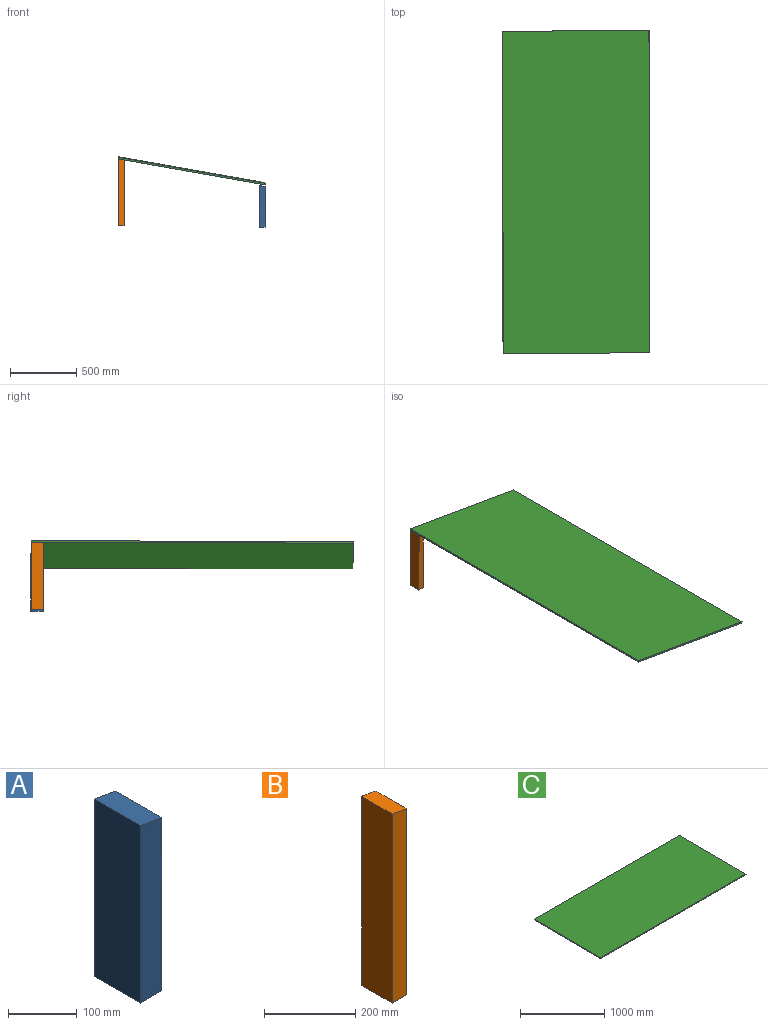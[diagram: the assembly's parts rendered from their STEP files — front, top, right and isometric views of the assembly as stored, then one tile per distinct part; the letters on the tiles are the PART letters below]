
ASSEMBLY  parts=3 mates=1
PART A: 6 faces, bbox 44.5x95.2x316.5 mm
  f0: plane 316.48x95.25mm, normal (-1,0,0), area 30144.9mm2, adj f1,f3,f4,f5
  f1: plane 95.25x44.45mm, normal (0.17,0,0.98), area 4299.2mm2, adj f0,f2,f3,f4
  f2: plane 308.65x95.25mm, normal (1,0,0), area 29398.3mm2, adj f1,f3,f4,f5
  f3: plane 316.48x44.45mm, normal (0,1,0), area 13893.7mm2, adj f0,f1,f2,f5
  f4: plane 316.48x44.45mm, normal (0,-1,0), area 13893.7mm2, adj f0,f1,f2,f5
  f5: plane 95.25x44.45mm, normal (0,0,-1), area 4233.9mm2, adj f0,f2,f3,f4
PART B: 6 faces, bbox 44.5x95.2x508 mm
  f0: plane 508x95.25mm, normal (-1,0,0), area 48386.9mm2, adj f1,f3,f4,f5
  f1: plane 95.25x44.45mm, normal (0,0,-1), area 4233.9mm2, adj f0,f2,f3,f4
  f2: plane 500.16x95.25mm, normal (1,0,0), area 47640.3mm2, adj f1,f3,f4,f5
  f3: plane 508x44.45mm, normal (0,1,0), area 22406.9mm2, adj f0,f1,f2,f5
  f4: plane 508x44.45mm, normal (0,-1,0), area 22406.9mm2, adj f0,f1,f2,f5
  f5: plane 95.25x44.45mm, normal (0.17,0,0.98), area 4299.3mm2, adj f0,f2,f3,f4
PART C: 6 faces, bbox 2438.4x1126x12.7 mm
  f0: plane 2438.4x1125.98mm, normal (0,0,1), area 2745596.9mm2, adj f2,f3,f4,f5
  f1: plane 2438.4x1125.98mm, normal (0,0,-1), area 2745596.9mm2, adj f2,f3,f4,f5
  f2: plane 1125.98x12.7mm, normal (1,0,0), area 14300mm2, adj f0,f1,f4,f5
  f3: plane 1125.98x12.7mm, normal (-1,0,0), area 14300mm2, adj f0,f1,f4,f5
  f4: plane 2438.4x12.7mm, normal (0,1,0), area 30967.7mm2, adj f0,f1,f2,f3
  f5: plane 2438.4x12.7mm, normal (0,-1,0), area 30967.7mm2, adj f0,f1,f2,f3
PLACE A rot(axis=(0.67,0,0.74),0.2deg) t=(484.37,1158.53,-149.9)mm
PLACE B rot(axis=(0.67,0,0.74),0.2deg) t=(-574.14,1121.31,-148.64)mm
PLACE C rot(axis=(-0.09,0.09,-0.99),90.3deg) t=(448.07,-1142.68,24.89)mm
MATE planar C.f1 <-> B.f5  axis (-0.17,0,-0.98) through (-596.57,1167.66,207.07)mm
